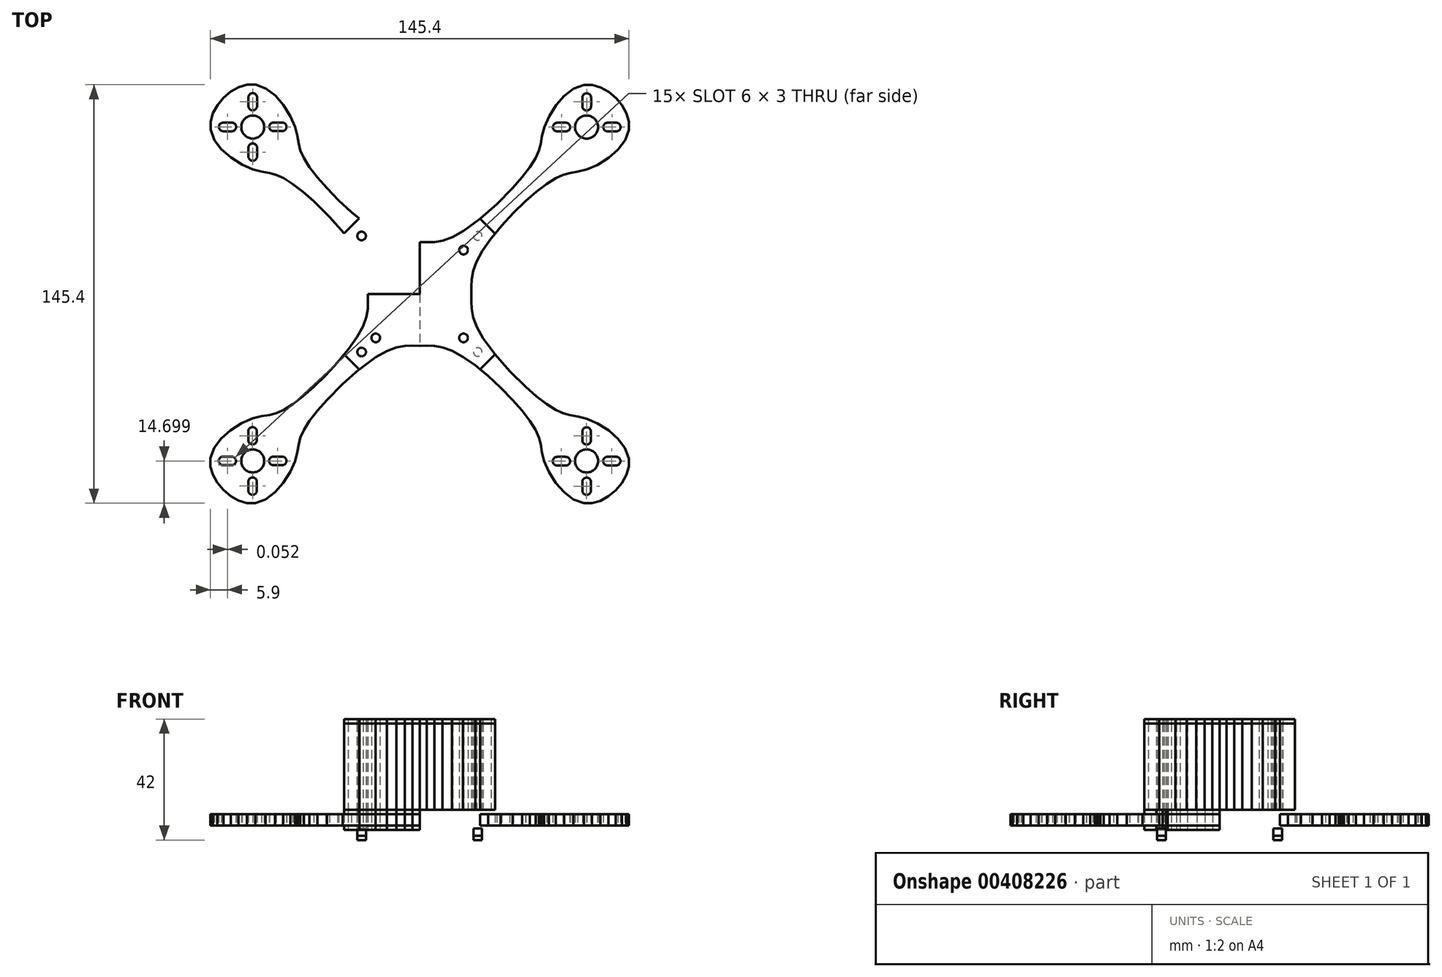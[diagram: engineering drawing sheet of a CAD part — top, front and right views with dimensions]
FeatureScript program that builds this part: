
annotation { "Feature Type Name" : "Feature", "Feature Type Description" : "" }
export const myFeature = defineFeature(function(context is Context, id is Id, definition is map)
    precondition{}
    {
        {
            var Q0;
            Q0=qCreatedBy(makeId("Top.planeOp"),FACE);
            var sketch = newSketch(context, id + "F0", { "sketchPlane" : qUnion([Q0])});
            skCircle(sketch, "E0", {"center": v(20.17, 20.17) * mm, "radius": 1.5 * mm});
            skLineSegment(sketch, "E1", {"start": v(26.23, 21) * mm, "end": v(21.02, 26.2) * mm});
            skLineSegment(sketch, "E2", {"start": v(0, 18) * mm, "end": v(2.5, 17.97) * mm});
            skLineSegment(sketch, "E3", {"start": v(2.5, 17.97) * mm, "end": v(5.15, 18.06) * mm});
            skLineSegment(sketch, "E4", {"start": v(5.15, 18.06) * mm, "end": v(8.09, 18.58) * mm});
            skLineSegment(sketch, "E5", {"start": v(8.09, 18.58) * mm, "end": v(11.44, 19.82) * mm});
            skLineSegment(sketch, "E6", {"start": v(11.44, 19.82) * mm, "end": v(15.32, 22) * mm});
            skLineSegment(sketch, "E7", {"start": v(15.32, 22) * mm, "end": v(20.97, 26.16) * mm});
            skLineSegment(sketch, "E8", {"start": v(20.97, 26.16) * mm, "end": v(26.8, 31.28) * mm});
            skLineSegment(sketch, "E9", {"start": v(26.8, 31.28) * mm, "end": v(32.27, 36.82) * mm});
            skLineSegment(sketch, "E10", {"start": v(32.27, 36.82) * mm, "end": v(35.55, 40.57) * mm});
            skLineSegment(sketch, "E11", {"start": v(35.55, 40.57) * mm, "end": v(38.27, 44.1) * mm});
            skLineSegment(sketch, "E12", {"start": v(38.27, 44.1) * mm, "end": v(40.27, 47.23) * mm});
            skLineSegment(sketch, "E13", {"start": v(40.27, 47.23) * mm, "end": v(41.45, 49.87) * mm});
            skLineSegment(sketch, "E14", {"start": v(41.45, 49.87) * mm, "end": v(42.05, 52.15) * mm});
            skLineSegment(sketch, "E15", {"start": v(42.05, 52.15) * mm, "end": v(42.52, 54.9) * mm});
            skLineSegment(sketch, "E16", {"start": v(42.52, 54.9) * mm, "end": v(43.3, 58) * mm});
            skLineSegment(sketch, "E17", {"start": v(43.3, 58) * mm, "end": v(44.94, 61.72) * mm});
            skLineSegment(sketch, "E18", {"start": v(44.94, 61.72) * mm, "end": v(47.43, 65.67) * mm});
            skLineSegment(sketch, "E19", {"start": v(47.43, 65.67) * mm, "end": v(50.24, 68.86) * mm});
            skLineSegment(sketch, "E20", {"start": v(50.24, 68.86) * mm, "end": v(53.5, 71.33) * mm});
            skLineSegment(sketch, "E21", {"start": v(53.5, 71.33) * mm, "end": v(57.12, 72.65) * mm});
            skLineSegment(sketch, "E22", {"start": v(57.12, 72.65) * mm, "end": v(59.99, 72.64) * mm});
            skLineSegment(sketch, "E23", {"start": v(59.99, 72.64) * mm, "end": v(62.89, 71.79) * mm});
            skLineSegment(sketch, "E24", {"start": v(62.89, 71.79) * mm, "end": v(65.67, 70.23) * mm});
            skLineSegment(sketch, "E25", {"start": v(65.67, 70.23) * mm, "end": v(68.19, 68.12) * mm});
            skLineSegment(sketch, "E26", {"start": v(68.19, 68.12) * mm, "end": v(70.3, 65.6) * mm});
            skLineSegment(sketch, "E27", {"start": v(70.3, 65.6) * mm, "end": v(71.85, 62.8) * mm});
            skLineSegment(sketch, "E28", {"start": v(71.85, 62.8) * mm, "end": v(72.7, 59.9) * mm});
            skLineSegment(sketch, "E29", {"start": v(72.7, 59.9) * mm, "end": v(72.7, 57.03) * mm});
            skLineSegment(sketch, "E30", {"start": v(72.7, 57.03) * mm, "end": v(71.38, 53.41) * mm});
            skLineSegment(sketch, "E31", {"start": v(71.38, 53.41) * mm, "end": v(68.9, 50.15) * mm});
            skLineSegment(sketch, "E32", {"start": v(68.9, 50.15) * mm, "end": v(65.7, 47.34) * mm});
            skLineSegment(sketch, "E33", {"start": v(65.7, 47.34) * mm, "end": v(61.77, 44.86) * mm});
            skLineSegment(sketch, "E34", {"start": v(61.77, 44.86) * mm, "end": v(58.04, 43.24) * mm});
            skLineSegment(sketch, "E35", {"start": v(58.04, 43.24) * mm, "end": v(54.95, 42.47) * mm});
            skLineSegment(sketch, "E36", {"start": v(54.95, 42.47) * mm, "end": v(52.18, 42.03) * mm});
            skLineSegment(sketch, "E37", {"start": v(52.18, 42.03) * mm, "end": v(49.88, 41.44) * mm});
            skLineSegment(sketch, "E38", {"start": v(49.88, 41.44) * mm, "end": v(47.23, 40.27) * mm});
            skLineSegment(sketch, "E39", {"start": v(47.23, 40.27) * mm, "end": v(44.09, 38.28) * mm});
            skLineSegment(sketch, "E40", {"start": v(44.09, 38.28) * mm, "end": v(40.55, 35.56) * mm});
            skLineSegment(sketch, "E41", {"start": v(40.55, 35.56) * mm, "end": v(36.8, 32.28) * mm});
            skLineSegment(sketch, "E42", {"start": v(36.8, 32.28) * mm, "end": v(32.56, 28.14) * mm});
            skLineSegment(sketch, "E43", {"start": v(32.56, 28.14) * mm, "end": v(28.48, 23.74) * mm});
            skLineSegment(sketch, "E44", {"start": v(28.48, 23.74) * mm, "end": v(24.82, 19.29) * mm});
            skLineSegment(sketch, "E45", {"start": v(24.82, 19.29) * mm, "end": v(21.82, 15.03) * mm});
            skLineSegment(sketch, "E46", {"start": v(21.82, 15.03) * mm, "end": v(19.7, 11.19) * mm});
            skLineSegment(sketch, "E47", {"start": v(19.7, 11.19) * mm, "end": v(18.54, 7.93) * mm});
            skLineSegment(sketch, "E48", {"start": v(18.54, 7.93) * mm, "end": v(18.06, 5.07) * mm});
            skLineSegment(sketch, "E49", {"start": v(18.06, 5.07) * mm, "end": v(17.97, 2.47) * mm});
            skLineSegment(sketch, "E50", {"start": v(17.97, 2.47) * mm, "end": v(18, 0) * mm});
            skArc(sketch, "E51", {"start": v(59.58, 50.75) * mm, "mid": v(58.08, 52.25) * mm, "end": v(56.58, 50.75) * mm});
            skArc(sketch, "E52", {"start": v(56.58, 47.75) * mm, "mid": v(58.08, 46.25) * mm, "end": v(59.58, 47.75) * mm});
            skLineSegment(sketch, "E53", {"start": v(59.48, 47.75) * mm, "end": v(59.48, 50.75) * mm});
            skLineSegment(sketch, "E54", {"start": v(56.58, 47.75) * mm, "end": v(56.58, 50.75) * mm});
            skArc(sketch, "E55", {"start": v(65.3, 59.5) * mm, "mid": v(63.8, 58) * mm, "end": v(65.3, 56.5) * mm});
            skArc(sketch, "E56", {"start": v(68.3, 56.5) * mm, "mid": v(69.8, 58) * mm, "end": v(68.3, 59.5) * mm});
            skLineSegment(sketch, "E57", {"start": v(68.3, 59.5) * mm, "end": v(65.3, 59.5) * mm});
            skLineSegment(sketch, "E58", {"start": v(68.3, 56.5) * mm, "end": v(65.3, 56.5) * mm});
            skArc(sketch, "E59", {"start": v(50.8, 56.5) * mm, "mid": v(52.3, 58) * mm, "end": v(50.8, 59.5) * mm});
            skArc(sketch, "E60", {"start": v(47.8, 59.5) * mm, "mid": v(46.3, 58) * mm, "end": v(47.8, 56.5) * mm});
            skLineSegment(sketch, "E61", {"start": v(47.8, 56.5) * mm, "end": v(50.8, 56.5) * mm});
            skLineSegment(sketch, "E62", {"start": v(47.8, 59.5) * mm, "end": v(50.8, 59.5) * mm});
            skArc(sketch, "E63", {"start": v(59.55, 68.25) * mm, "mid": v(58.05, 69.75) * mm, "end": v(56.55, 68.25) * mm});
            skArc(sketch, "E64", {"start": v(56.55, 65.25) * mm, "mid": v(58.05, 63.75) * mm, "end": v(59.55, 65.25) * mm});
            skLineSegment(sketch, "E65", {"start": v(59.55, 65.25) * mm, "end": v(59.55, 68.25) * mm});
            skLineSegment(sketch, "E66", {"start": v(56.55, 65.25) * mm, "end": v(56.55, 68.25) * mm});
            skCircle(sketch, "E67", {"center": v(58, 58) * mm, "radius": 4 * mm});
            skCircle(sketch, "E68", {"center": v(20.17, -20.17) * mm, "radius": 1.5 * mm});
            skCircle(sketch, "E69", {"center": v(-20.17, 20.17) * mm, "radius": 1.5 * mm});
            skLineSegment(sketch, "E70", {"start": v(-21, 26.23) * mm, "end": v(-26.2, 21.02) * mm});
            skLineSegment(sketch, "E71", {"start": v(-18, 0) * mm, "end": v(-17.97, 2.5) * mm});
            skLineSegment(sketch, "E72", {"start": v(-17.97, 2.5) * mm, "end": v(-18.06, 5.15) * mm});
            skLineSegment(sketch, "E73", {"start": v(-18.06, 5.15) * mm, "end": v(-18.58, 8.09) * mm});
            skLineSegment(sketch, "E74", {"start": v(-18.58, 8.09) * mm, "end": v(-19.81, 11.44) * mm});
            skLineSegment(sketch, "E75", {"start": v(-19.81, 11.44) * mm, "end": v(-22, 15.32) * mm});
            skLineSegment(sketch, "E76", {"start": v(-22, 15.32) * mm, "end": v(-26.16, 20.97) * mm});
            skLineSegment(sketch, "E77", {"start": v(-26.16, 20.97) * mm, "end": v(-31.28, 26.8) * mm});
            skLineSegment(sketch, "E78", {"start": v(-31.28, 26.8) * mm, "end": v(-36.82, 32.27) * mm});
            skLineSegment(sketch, "E79", {"start": v(-36.82, 32.27) * mm, "end": v(-40.57, 35.55) * mm});
            skLineSegment(sketch, "E80", {"start": v(-40.57, 35.55) * mm, "end": v(-44.1, 38.27) * mm});
            skLineSegment(sketch, "E81", {"start": v(-44.1, 38.27) * mm, "end": v(-47.23, 40.27) * mm});
            skLineSegment(sketch, "E82", {"start": v(-47.23, 40.27) * mm, "end": v(-49.87, 41.45) * mm});
            skLineSegment(sketch, "E83", {"start": v(-49.87, 41.45) * mm, "end": v(-52.15, 42.05) * mm});
            skLineSegment(sketch, "E84", {"start": v(-52.15, 42.05) * mm, "end": v(-54.9, 42.52) * mm});
            skLineSegment(sketch, "E85", {"start": v(-54.9, 42.52) * mm, "end": v(-58, 43.3) * mm});
            skLineSegment(sketch, "E86", {"start": v(-58, 43.3) * mm, "end": v(-61.72, 44.94) * mm});
            skLineSegment(sketch, "E87", {"start": v(-61.72, 44.94) * mm, "end": v(-65.66, 47.43) * mm});
            skLineSegment(sketch, "E88", {"start": v(-65.66, 47.43) * mm, "end": v(-68.86, 50.24) * mm});
            skLineSegment(sketch, "E89", {"start": v(-68.86, 50.24) * mm, "end": v(-71.33, 53.5) * mm});
            skLineSegment(sketch, "E90", {"start": v(-71.33, 53.5) * mm, "end": v(-72.65, 57.12) * mm});
            skLineSegment(sketch, "E91", {"start": v(-72.65, 57.12) * mm, "end": v(-72.64, 60) * mm});
            skLineSegment(sketch, "E92", {"start": v(-72.64, 60) * mm, "end": v(-71.79, 62.9) * mm});
            skLineSegment(sketch, "E93", {"start": v(-71.79, 62.9) * mm, "end": v(-70.23, 65.67) * mm});
            skLineSegment(sketch, "E94", {"start": v(-70.23, 65.67) * mm, "end": v(-68.12, 68.2) * mm});
            skLineSegment(sketch, "E95", {"start": v(-68.12, 68.2) * mm, "end": v(-65.6, 70.3) * mm});
            skLineSegment(sketch, "E96", {"start": v(-65.6, 70.3) * mm, "end": v(-62.8, 71.85) * mm});
            skLineSegment(sketch, "E97", {"start": v(-62.8, 71.85) * mm, "end": v(-59.9, 72.7) * mm});
            skLineSegment(sketch, "E98", {"start": v(-59.9, 72.7) * mm, "end": v(-57.03, 72.7) * mm});
            skLineSegment(sketch, "E99", {"start": v(-57.03, 72.7) * mm, "end": v(-53.41, 71.38) * mm});
            skLineSegment(sketch, "E100", {"start": v(-53.41, 71.38) * mm, "end": v(-50.15, 68.9) * mm});
            skLineSegment(sketch, "E101", {"start": v(-50.15, 68.9) * mm, "end": v(-47.34, 65.7) * mm});
            skLineSegment(sketch, "E102", {"start": v(-47.34, 65.7) * mm, "end": v(-44.86, 61.77) * mm});
            skLineSegment(sketch, "E103", {"start": v(-44.86, 61.77) * mm, "end": v(-43.23, 58.04) * mm});
            skLineSegment(sketch, "E104", {"start": v(-43.23, 58.04) * mm, "end": v(-42.47, 54.95) * mm});
            skLineSegment(sketch, "E105", {"start": v(-42.47, 54.95) * mm, "end": v(-42.03, 52.18) * mm});
            skLineSegment(sketch, "E106", {"start": v(-42.03, 52.18) * mm, "end": v(-41.44, 49.88) * mm});
            skLineSegment(sketch, "E107", {"start": v(-41.44, 49.88) * mm, "end": v(-40.27, 47.23) * mm});
            skLineSegment(sketch, "E108", {"start": v(-40.27, 47.23) * mm, "end": v(-38.28, 44.09) * mm});
            skLineSegment(sketch, "E109", {"start": v(-38.28, 44.09) * mm, "end": v(-35.56, 40.55) * mm});
            skLineSegment(sketch, "E110", {"start": v(-35.56, 40.55) * mm, "end": v(-32.28, 36.8) * mm});
            skLineSegment(sketch, "E111", {"start": v(-32.28, 36.8) * mm, "end": v(-28.14, 32.56) * mm});
            skLineSegment(sketch, "E112", {"start": v(-28.14, 32.56) * mm, "end": v(-23.73, 28.48) * mm});
            skLineSegment(sketch, "E113", {"start": v(-23.73, 28.48) * mm, "end": v(-19.29, 24.83) * mm});
            skLineSegment(sketch, "E114", {"start": v(-19.29, 24.83) * mm, "end": v(-15.03, 21.82) * mm});
            skLineSegment(sketch, "E115", {"start": v(-15.03, 21.82) * mm, "end": v(-11.19, 19.7) * mm});
            skLineSegment(sketch, "E116", {"start": v(-11.19, 19.7) * mm, "end": v(-7.93, 18.54) * mm});
            skLineSegment(sketch, "E117", {"start": v(-7.93, 18.54) * mm, "end": v(-5.07, 18.06) * mm});
            skLineSegment(sketch, "E118", {"start": v(-5.07, 18.06) * mm, "end": v(-2.47, 17.97) * mm});
            skLineSegment(sketch, "E119", {"start": v(-2.47, 17.97) * mm, "end": v(0, 18) * mm});
            skArc(sketch, "E120", {"start": v(-50.75, 59.58) * mm, "mid": v(-52.25, 58.08) * mm, "end": v(-50.75, 56.58) * mm});
            skArc(sketch, "E121", {"start": v(-47.75, 56.58) * mm, "mid": v(-46.25, 58.08) * mm, "end": v(-47.75, 59.58) * mm});
            skLineSegment(sketch, "E122", {"start": v(-47.75, 59.58) * mm, "end": v(-50.75, 59.58) * mm});
            skLineSegment(sketch, "E123", {"start": v(-47.75, 56.58) * mm, "end": v(-50.75, 56.58) * mm});
            skArc(sketch, "E124", {"start": v(-59.5, 65.3) * mm, "mid": v(-58, 63.8) * mm, "end": v(-56.5, 65.3) * mm});
            skArc(sketch, "E125", {"start": v(-56.5, 68.3) * mm, "mid": v(-58, 69.8) * mm, "end": v(-59.5, 68.3) * mm});
            skLineSegment(sketch, "E126", {"start": v(-59.5, 68.3) * mm, "end": v(-59.5, 65.3) * mm});
            skLineSegment(sketch, "E127", {"start": v(-56.5, 68.3) * mm, "end": v(-56.5, 65.3) * mm});
            skArc(sketch, "E128", {"start": v(-56.5, 50.8) * mm, "mid": v(-58, 52.3) * mm, "end": v(-59.5, 50.8) * mm});
            skArc(sketch, "E129", {"start": v(-59.5, 47.8) * mm, "mid": v(-58, 46.3) * mm, "end": v(-56.5, 47.8) * mm});
            skLineSegment(sketch, "E130", {"start": v(-56.5, 47.8) * mm, "end": v(-56.5, 50.8) * mm});
            skLineSegment(sketch, "E131", {"start": v(-59.5, 47.8) * mm, "end": v(-59.5, 50.8) * mm});
            skArc(sketch, "E132", {"start": v(-68.25, 59.55) * mm, "mid": v(-69.75, 58.05) * mm, "end": v(-68.25, 56.55) * mm});
            skArc(sketch, "E133", {"start": v(-65.25, 56.55) * mm, "mid": v(-63.75, 58.05) * mm, "end": v(-65.25, 59.55) * mm});
            skLineSegment(sketch, "E134", {"start": v(-65.25, 59.55) * mm, "end": v(-68.25, 59.55) * mm});
            skLineSegment(sketch, "E135", {"start": v(-65.25, 56.55) * mm, "end": v(-68.25, 56.55) * mm});
            skCircle(sketch, "E136", {"center": v(-58, 58) * mm, "radius": 4 * mm});
            skLineSegment(sketch, "E137", {"start": v(20.99, -26.22) * mm, "end": v(26.2, -21.02) * mm});
            skLineSegment(sketch, "E138", {"start": v(18, 0) * mm, "end": v(17.97, -2.5) * mm});
            skLineSegment(sketch, "E139", {"start": v(17.97, -2.5) * mm, "end": v(18.07, -5.15) * mm});
            skLineSegment(sketch, "E140", {"start": v(18.07, -5.15) * mm, "end": v(18.58, -8.09) * mm});
            skLineSegment(sketch, "E141", {"start": v(18.58, -8.09) * mm, "end": v(19.82, -11.44) * mm});
            skLineSegment(sketch, "E142", {"start": v(19.82, -11.44) * mm, "end": v(22.01, -15.32) * mm});
            skLineSegment(sketch, "E143", {"start": v(22.01, -15.32) * mm, "end": v(26.16, -20.97) * mm});
            skLineSegment(sketch, "E144", {"start": v(26.16, -20.97) * mm, "end": v(31.28, -26.8) * mm});
            skLineSegment(sketch, "E145", {"start": v(31.28, -26.8) * mm, "end": v(36.82, -32.27) * mm});
            skLineSegment(sketch, "E146", {"start": v(36.82, -32.27) * mm, "end": v(40.57, -35.55) * mm});
            skLineSegment(sketch, "E147", {"start": v(40.57, -35.55) * mm, "end": v(44.1, -38.27) * mm});
            skLineSegment(sketch, "E148", {"start": v(44.1, -38.27) * mm, "end": v(47.24, -40.27) * mm});
            skLineSegment(sketch, "E149", {"start": v(47.24, -40.27) * mm, "end": v(49.87, -41.45) * mm});
            skLineSegment(sketch, "E150", {"start": v(49.87, -41.45) * mm, "end": v(52.16, -42.05) * mm});
            skLineSegment(sketch, "E151", {"start": v(52.16, -42.05) * mm, "end": v(54.9, -42.52) * mm});
            skLineSegment(sketch, "E152", {"start": v(54.9, -42.52) * mm, "end": v(58, -43.3) * mm});
            skLineSegment(sketch, "E153", {"start": v(58, -43.3) * mm, "end": v(61.72, -44.94) * mm});
            skLineSegment(sketch, "E154", {"start": v(61.72, -44.94) * mm, "end": v(65.67, -47.43) * mm});
            skLineSegment(sketch, "E155", {"start": v(65.67, -47.43) * mm, "end": v(68.87, -50.24) * mm});
            skLineSegment(sketch, "E156", {"start": v(68.87, -50.24) * mm, "end": v(71.34, -53.5) * mm});
            skLineSegment(sketch, "E157", {"start": v(71.34, -53.5) * mm, "end": v(72.65, -57.12) * mm});
            skLineSegment(sketch, "E158", {"start": v(72.65, -57.12) * mm, "end": v(72.64, -60) * mm});
            skLineSegment(sketch, "E159", {"start": v(72.64, -60) * mm, "end": v(71.79, -62.9) * mm});
            skLineSegment(sketch, "E160", {"start": v(71.79, -62.9) * mm, "end": v(70.23, -65.67) * mm});
            skLineSegment(sketch, "E161", {"start": v(70.23, -65.67) * mm, "end": v(68.12, -68.2) * mm});
            skLineSegment(sketch, "E162", {"start": v(68.12, -68.2) * mm, "end": v(65.6, -70.3) * mm});
            skLineSegment(sketch, "E163", {"start": v(65.6, -70.3) * mm, "end": v(62.8, -71.85) * mm});
            skLineSegment(sketch, "E164", {"start": v(62.8, -71.85) * mm, "end": v(59.9, -72.7) * mm});
            skLineSegment(sketch, "E165", {"start": v(59.9, -72.7) * mm, "end": v(57.03, -72.7) * mm});
            skLineSegment(sketch, "E166", {"start": v(57.03, -72.7) * mm, "end": v(53.41, -71.38) * mm});
            skLineSegment(sketch, "E167", {"start": v(53.41, -71.38) * mm, "end": v(50.15, -68.9) * mm});
            skLineSegment(sketch, "E168", {"start": v(50.15, -68.9) * mm, "end": v(47.34, -65.7) * mm});
            skLineSegment(sketch, "E169", {"start": v(47.34, -65.7) * mm, "end": v(44.86, -61.77) * mm});
            skLineSegment(sketch, "E170", {"start": v(44.86, -61.77) * mm, "end": v(43.24, -58.04) * mm});
            skLineSegment(sketch, "E171", {"start": v(43.24, -58.04) * mm, "end": v(42.47, -54.95) * mm});
            skLineSegment(sketch, "E172", {"start": v(42.47, -54.95) * mm, "end": v(42.03, -52.18) * mm});
            skLineSegment(sketch, "E173", {"start": v(42.03, -52.18) * mm, "end": v(41.44, -49.88) * mm});
            skLineSegment(sketch, "E174", {"start": v(41.44, -49.88) * mm, "end": v(40.27, -47.23) * mm});
            skLineSegment(sketch, "E175", {"start": v(40.27, -47.23) * mm, "end": v(38.28, -44.09) * mm});
            skLineSegment(sketch, "E176", {"start": v(38.28, -44.09) * mm, "end": v(35.56, -40.55) * mm});
            skLineSegment(sketch, "E177", {"start": v(35.56, -40.55) * mm, "end": v(32.28, -36.8) * mm});
            skLineSegment(sketch, "E178", {"start": v(32.28, -36.8) * mm, "end": v(28.14, -32.56) * mm});
            skLineSegment(sketch, "E179", {"start": v(28.14, -32.56) * mm, "end": v(23.74, -28.48) * mm});
            skLineSegment(sketch, "E180", {"start": v(23.74, -28.48) * mm, "end": v(19.29, -24.83) * mm});
            skLineSegment(sketch, "E181", {"start": v(19.29, -24.83) * mm, "end": v(15.03, -21.82) * mm});
            skLineSegment(sketch, "E182", {"start": v(15.03, -21.82) * mm, "end": v(11.2, -19.7) * mm});
            skLineSegment(sketch, "E183", {"start": v(11.2, -19.7) * mm, "end": v(7.93, -18.54) * mm});
            skLineSegment(sketch, "E184", {"start": v(7.93, -18.54) * mm, "end": v(5.07, -18.06) * mm});
            skLineSegment(sketch, "E185", {"start": v(5.07, -18.06) * mm, "end": v(2.47, -17.97) * mm});
            skLineSegment(sketch, "E186", {"start": v(2.47, -17.97) * mm, "end": v(0, -18) * mm});
            skArc(sketch, "E187", {"start": v(50.75, -59.58) * mm, "mid": v(52.25, -58.08) * mm, "end": v(50.75, -56.58) * mm});
            skArc(sketch, "E188", {"start": v(47.75, -56.58) * mm, "mid": v(46.25, -58.08) * mm, "end": v(47.75, -59.58) * mm});
            skLineSegment(sketch, "E189", {"start": v(47.75, -59.58) * mm, "end": v(50.75, -59.58) * mm});
            skLineSegment(sketch, "E190", {"start": v(47.75, -56.58) * mm, "end": v(50.75, -56.58) * mm});
            skArc(sketch, "E191", {"start": v(59.5, -65.3) * mm, "mid": v(58, -63.8) * mm, "end": v(56.5, -65.3) * mm});
            skArc(sketch, "E192", {"start": v(56.5, -68.3) * mm, "mid": v(58, -69.8) * mm, "end": v(59.5, -68.3) * mm});
            skLineSegment(sketch, "E193", {"start": v(59.5, -68.3) * mm, "end": v(59.5, -65.3) * mm});
            skLineSegment(sketch, "E194", {"start": v(56.5, -68.3) * mm, "end": v(56.5, -65.3) * mm});
            skArc(sketch, "E195", {"start": v(56.5, -50.8) * mm, "mid": v(58, -52.3) * mm, "end": v(59.5, -50.8) * mm});
            skArc(sketch, "E196", {"start": v(59.5, -47.8) * mm, "mid": v(58, -46.3) * mm, "end": v(56.5, -47.8) * mm});
            skLineSegment(sketch, "E197", {"start": v(56.5, -47.8) * mm, "end": v(56.5, -50.8) * mm});
            skLineSegment(sketch, "E198", {"start": v(59.5, -47.8) * mm, "end": v(59.5, -50.8) * mm});
            skArc(sketch, "E199", {"start": v(68.25, -59.55) * mm, "mid": v(69.75, -58.05) * mm, "end": v(68.25, -56.55) * mm});
            skArc(sketch, "E200", {"start": v(65.25, -56.55) * mm, "mid": v(63.75, -58.05) * mm, "end": v(65.25, -59.55) * mm});
            skLineSegment(sketch, "E201", {"start": v(65.25, -59.55) * mm, "end": v(68.25, -59.55) * mm});
            skLineSegment(sketch, "E202", {"start": v(65.25, -56.55) * mm, "end": v(68.25, -56.55) * mm});
            skCircle(sketch, "E203", {"center": v(58, -58) * mm, "radius": 4 * mm});
            skLineSegment(sketch, "E204", {"start": v(-18, 0) * mm, "end": v(0, 0) * mm});
            skLineSegment(sketch, "E205", {"start": v(-26.23, -21) * mm, "end": v(-21.02, -26.2) * mm});
            skLineSegment(sketch, "E206", {"start": v(0, -18) * mm, "end": v(-2.5, -17.97) * mm});
            skLineSegment(sketch, "E207", {"start": v(-2.5, -17.97) * mm, "end": v(-5.15, -18.06) * mm});
            skLineSegment(sketch, "E208", {"start": v(-5.15, -18.06) * mm, "end": v(-8.09, -18.58) * mm});
            skLineSegment(sketch, "E209", {"start": v(-8.09, -18.58) * mm, "end": v(-11.44, -19.82) * mm});
            skLineSegment(sketch, "E210", {"start": v(-11.44, -19.82) * mm, "end": v(-15.32, -22) * mm});
            skLineSegment(sketch, "E211", {"start": v(-15.32, -22) * mm, "end": v(-20.97, -26.16) * mm});
            skLineSegment(sketch, "E212", {"start": v(-20.97, -26.16) * mm, "end": v(-26.8, -31.28) * mm});
            skLineSegment(sketch, "E213", {"start": v(-26.8, -31.28) * mm, "end": v(-32.27, -36.82) * mm});
            skLineSegment(sketch, "E214", {"start": v(-32.27, -36.82) * mm, "end": v(-35.55, -40.57) * mm});
            skLineSegment(sketch, "E215", {"start": v(-35.55, -40.57) * mm, "end": v(-38.27, -44.1) * mm});
            skLineSegment(sketch, "E216", {"start": v(-38.27, -44.1) * mm, "end": v(-40.27, -47.23) * mm});
            skLineSegment(sketch, "E217", {"start": v(-40.27, -47.23) * mm, "end": v(-41.45, -49.87) * mm});
            skLineSegment(sketch, "E218", {"start": v(-41.45, -49.87) * mm, "end": v(-42.05, -52.15) * mm});
            skLineSegment(sketch, "E219", {"start": v(-42.05, -52.15) * mm, "end": v(-42.52, -54.9) * mm});
            skLineSegment(sketch, "E220", {"start": v(-42.52, -54.9) * mm, "end": v(-43.3, -58) * mm});
            skLineSegment(sketch, "E221", {"start": v(-43.3, -58) * mm, "end": v(-44.94, -61.72) * mm});
            skLineSegment(sketch, "E222", {"start": v(-44.94, -61.72) * mm, "end": v(-47.43, -65.67) * mm});
            skLineSegment(sketch, "E223", {"start": v(-47.43, -65.67) * mm, "end": v(-50.24, -68.86) * mm});
            skLineSegment(sketch, "E224", {"start": v(-50.24, -68.86) * mm, "end": v(-53.5, -71.33) * mm});
            skLineSegment(sketch, "E225", {"start": v(-53.5, -71.33) * mm, "end": v(-57.12, -72.65) * mm});
            skLineSegment(sketch, "E226", {"start": v(-57.12, -72.65) * mm, "end": v(-59.99, -72.64) * mm});
            skLineSegment(sketch, "E227", {"start": v(-59.99, -72.64) * mm, "end": v(-62.89, -71.79) * mm});
            skLineSegment(sketch, "E228", {"start": v(-62.89, -71.79) * mm, "end": v(-65.67, -70.23) * mm});
            skLineSegment(sketch, "E229", {"start": v(-65.67, -70.23) * mm, "end": v(-68.19, -68.12) * mm});
            skLineSegment(sketch, "E230", {"start": v(-68.19, -68.12) * mm, "end": v(-70.3, -65.6) * mm});
            skLineSegment(sketch, "E231", {"start": v(-70.3, -65.6) * mm, "end": v(-71.85, -62.8) * mm});
            skLineSegment(sketch, "E232", {"start": v(-71.85, -62.8) * mm, "end": v(-72.7, -59.9) * mm});
            skLineSegment(sketch, "E233", {"start": v(-72.7, -59.9) * mm, "end": v(-72.7, -57.03) * mm});
            skLineSegment(sketch, "E234", {"start": v(-72.7, -57.03) * mm, "end": v(-71.38, -53.41) * mm});
            skLineSegment(sketch, "E235", {"start": v(-71.38, -53.41) * mm, "end": v(-68.9, -50.15) * mm});
            skLineSegment(sketch, "E236", {"start": v(-68.9, -50.15) * mm, "end": v(-65.7, -47.34) * mm});
            skLineSegment(sketch, "E237", {"start": v(-65.7, -47.34) * mm, "end": v(-61.77, -44.86) * mm});
            skLineSegment(sketch, "E238", {"start": v(-61.77, -44.86) * mm, "end": v(-58.04, -43.24) * mm});
            skLineSegment(sketch, "E239", {"start": v(-58.04, -43.24) * mm, "end": v(-54.95, -42.47) * mm});
            skLineSegment(sketch, "E240", {"start": v(-54.95, -42.47) * mm, "end": v(-52.18, -42.03) * mm});
            skLineSegment(sketch, "E241", {"start": v(-52.18, -42.03) * mm, "end": v(-49.88, -41.44) * mm});
            skLineSegment(sketch, "E242", {"start": v(-49.88, -41.44) * mm, "end": v(-47.23, -40.27) * mm});
            skLineSegment(sketch, "E243", {"start": v(-47.23, -40.27) * mm, "end": v(-44.09, -38.28) * mm});
            skLineSegment(sketch, "E244", {"start": v(-44.09, -38.28) * mm, "end": v(-40.55, -35.56) * mm});
            skLineSegment(sketch, "E245", {"start": v(-40.55, -35.56) * mm, "end": v(-36.8, -32.28) * mm});
            skLineSegment(sketch, "E246", {"start": v(-36.8, -32.28) * mm, "end": v(-32.56, -28.14) * mm});
            skLineSegment(sketch, "E247", {"start": v(-32.56, -28.14) * mm, "end": v(-28.48, -23.74) * mm});
            skLineSegment(sketch, "E248", {"start": v(-28.48, -23.74) * mm, "end": v(-24.82, -19.29) * mm});
            skLineSegment(sketch, "E249", {"start": v(-24.82, -19.29) * mm, "end": v(-21.82, -15.03) * mm});
            skLineSegment(sketch, "E250", {"start": v(-21.82, -15.03) * mm, "end": v(-19.7, -11.19) * mm});
            skLineSegment(sketch, "E251", {"start": v(-19.7, -11.19) * mm, "end": v(-18.54, -7.93) * mm});
            skLineSegment(sketch, "E252", {"start": v(-18.54, -7.93) * mm, "end": v(-18.06, -5.07) * mm});
            skLineSegment(sketch, "E253", {"start": v(-18.06, -5.07) * mm, "end": v(-17.97, -2.47) * mm});
            skLineSegment(sketch, "E254", {"start": v(-17.97, -2.47) * mm, "end": v(-18, 0) * mm});
            skArc(sketch, "E255", {"start": v(-59.58, -50.75) * mm, "mid": v(-58.08, -52.25) * mm, "end": v(-56.58, -50.75) * mm});
            skArc(sketch, "E256", {"start": v(-56.58, -47.75) * mm, "mid": v(-58.08, -46.25) * mm, "end": v(-59.58, -47.75) * mm});
            skLineSegment(sketch, "E257", {"start": v(-59.58, -47.75) * mm, "end": v(-59.58, -50.75) * mm});
            skLineSegment(sketch, "E258", {"start": v(-56.58, -47.75) * mm, "end": v(-56.58, -50.75) * mm});
            skArc(sketch, "E259", {"start": v(-65.3, -59.5) * mm, "mid": v(-63.8, -58) * mm, "end": v(-65.3, -56.5) * mm});
            skArc(sketch, "E260", {"start": v(-68.3, -56.5) * mm, "mid": v(-69.8, -58) * mm, "end": v(-68.3, -59.5) * mm});
            skLineSegment(sketch, "E261", {"start": v(-68.3, -59.5) * mm, "end": v(-65.3, -59.5) * mm});
            skLineSegment(sketch, "E262", {"start": v(-68.3, -56.5) * mm, "end": v(-65.3, -56.5) * mm});
            skArc(sketch, "E263", {"start": v(-50.8, -56.5) * mm, "mid": v(-52.3, -58) * mm, "end": v(-50.8, -59.5) * mm});
            skArc(sketch, "E264", {"start": v(-47.8, -59.5) * mm, "mid": v(-46.3, -58) * mm, "end": v(-47.8, -56.5) * mm});
            skLineSegment(sketch, "E265", {"start": v(-47.8, -56.5) * mm, "end": v(-50.8, -56.5) * mm});
            skLineSegment(sketch, "E266", {"start": v(-47.8, -59.5) * mm, "end": v(-50.8, -59.5) * mm});
            skArc(sketch, "E267", {"start": v(-59.55, -68.25) * mm, "mid": v(-58.05, -69.75) * mm, "end": v(-56.55, -68.25) * mm});
            skArc(sketch, "E268", {"start": v(-56.55, -65.25) * mm, "mid": v(-58.05, -63.75) * mm, "end": v(-59.55, -65.25) * mm});
            skLineSegment(sketch, "E269", {"start": v(-59.55, -65.25) * mm, "end": v(-59.55, -68.25) * mm});
            skLineSegment(sketch, "E270", {"start": v(-56.55, -65.25) * mm, "end": v(-56.55, -68.25) * mm});
            skCircle(sketch, "E271", {"center": v(-58, -58) * mm, "radius": 4 * mm});
            skLineSegment(sketch, "E272", {"start": v(0, 0) * mm, "end": v(0, -18) * mm});
            skCircle(sketch, "E273", {"center": v(-20.17, -20.17) * mm, "radius": 1.5 * mm});
            skCircle(sketch, "E274", {"center": v(15.25, 15.25) * mm, "radius": 1.5 * mm});
            skCircle(sketch, "E275", {"center": v(15.25, -15.25) * mm, "radius": 1.5 * mm});
            skCircle(sketch, "E276", {"center": v(-15.25, -15.25) * mm, "radius": 1.5 * mm});
            skCircle(sketch, "E277", {"center": v(-15.25, 16.63) * mm, "radius": 1.5 * mm});
            skLineSegment(sketch, "E278", {"start": v(0, 0) * mm, "end": v(0, 18) * mm});
            skLineSegment(sketch, "E279", {"start": v(0, 0) * mm, "end": v(18, 0) * mm});
            skPoint(sketch, "E280", {"position": v(-15.25, -10.25) * mm});
            skLineSegment(sketch, "E281.top", {"start": v(-15.06, 0) * mm, "end": v(-12.17, 0) * mm});
            skPoint(sketch, "E282", {"position": v(49.3, 58) * mm});
            skSolve(sketch);
        }
        {
            var Q0;
            {var subQ1=sQuery(id+"F0.wireOp",EDGE,"E205");Q0=makeQuery(id+"F0.imprint","IMPRINT",FACE,{"disambiguationData":[TD([[makeQuery(id+"F0.imprint","IMPRINT",EDGE,{"derivedFrom":subQ1}),1.0]])]});}
            var Q1;
            {var subQ1=sQuery(id+"F0.wireOp",EDGE,"E205");Q1=makeQuery(id+"F0.imprint","IMPRINT",FACE,{"disambiguationData":[TD([[makeQuery(id+"F0.imprint","IMPRINT",EDGE,{"derivedFrom":subQ1}),-1.0]])]});}
            extrude(context, id + "F1", {"entities" : qUnion([Q0, Q1]), "depth" : 4 * mm});
        }
        {
            var Q0;
            Q0=makeQuery(id+"F0.imprint","IMPRINT",FACE,{"disambiguationData":[TD([[makeQuery(id+"F0.imprint","IMPRINT",EDGE,{"derivedFrom":sQuery(id+"F0.wireOp",EDGE,"E69")}),1.0]])]});
            var Q1;
            {var subQ1=sQuery(id+"F0.wireOp",EDGE,"E70");Q1=makeQuery(id+"F0.imprint","IMPRINT",FACE,{"disambiguationData":[TD([[makeQuery(id+"F0.imprint","IMPRINT",EDGE,{"derivedFrom":subQ1}),-1.0]])]});}
            extrude(context, id + "F2", {"entities" : qUnion([Q0, Q1]), "depth" : 4 * mm});
        }
        {
            var Q0;
            Q0=makeQuery(id+"F0.imprint","IMPRINT",FACE,{"disambiguationData":[TD([[makeQuery(id+"F0.imprint","IMPRINT",EDGE,{"derivedFrom":sQuery(id+"F0.wireOp",EDGE,"E0")}),1.0]])]});
            var Q1;
            {var subQ1=sQuery(id+"F0.wireOp",EDGE,"E1");Q1=makeQuery(id+"F0.imprint","IMPRINT",FACE,{"disambiguationData":[TD([[makeQuery(id+"F0.imprint","IMPRINT",EDGE,{"derivedFrom":subQ1}),-1.0]])]});}
            extrude(context, id + "F3", {"entities" : qUnion([Q0, Q1]), "depth" : 4 * mm});
        }
        {
            var Q0;
            Q0=makeQuery(id+"F0.imprint","IMPRINT",FACE,{"disambiguationData":[TD([[makeQuery(id+"F0.imprint","IMPRINT",EDGE,{"derivedFrom":sQuery(id+"F0.wireOp",EDGE,"E68")}),1.0]])]});
            var Q1;
            {var subQ1=sQuery(id+"F0.wireOp",EDGE,"E137");Q1=makeQuery(id+"F0.imprint","IMPRINT",FACE,{"disambiguationData":[TD([[makeQuery(id+"F0.imprint","IMPRINT",EDGE,{"derivedFrom":subQ1}),-1.0]])]});}
            extrude(context, id + "F4", {"entities" : qUnion([Q0, Q1]), "depth" : 4 * mm});
        }
        {
            var Q0;
            Q0=makeQuery(id+"F0.imprint","IMPRINT",FACE,{"disambiguationData":[TD([[makeQuery(id+"F0.imprint","IMPRINT",EDGE,{"derivedFrom":sQuery(id+"F0.wireOp",EDGE,"E69")}),1.0]])]});
            var Q1;
            Q1=makeQuery(id+"F0.imprint","IMPRINT",FACE,{"disambiguationData":[TD([[makeQuery(id+"F0.imprint","IMPRINT",EDGE,{"derivedFrom":sQuery(id+"F0.wireOp",EDGE,"E0")}),1.0]])]});
            var Q2;
            Q2=makeQuery(id+"F0.imprint","IMPRINT",FACE,{"disambiguationData":[TD([[makeQuery(id+"F0.imprint","IMPRINT",EDGE,{"derivedFrom":sQuery(id+"F0.wireOp",EDGE,"E68")}),1.0]])]});
            var Q3;
            {var subQ1=sQuery(id+"F0.wireOp",EDGE,"E205");Q3=makeQuery(id+"F0.imprint","IMPRINT",FACE,{"disambiguationData":[TD([[makeQuery(id+"F0.imprint","IMPRINT",EDGE,{"derivedFrom":subQ1}),1.0]])]});}
            extrude(context, id + "F5", {"entities" : qUnion([Q0, Q1, Q2, Q3]), "depth" : 1.5 * mm});
        }
        {
            var Q0;
            Q0=makeQuery(id+"F5.opExtrude","CAP_FACE",FACE,{"disambiguationData":[OSD([sQuery(id+"F0.wireOp",EDGE,"E0"),sQuery(id+"F0.wireOp",EDGE,"E1"),sQuery(id+"F0.wireOp",EDGE,"E2"),sQuery(id+"F0.wireOp",EDGE,"E3"),sQuery(id+"F0.wireOp",EDGE,"E4"),sQuery(id+"F0.wireOp",EDGE,"E5"),sQuery(id+"F0.wireOp",EDGE,"E6"),sQuery(id+"F0.wireOp",EDGE,"E7"),sQuery(id+"F0.wireOp",EDGE,"E8"),sQuery(id+"F0.wireOp",EDGE,"E44"),sQuery(id+"F0.wireOp",EDGE,"E45"),sQuery(id+"F0.wireOp",EDGE,"E46"),sQuery(id+"F0.wireOp",EDGE,"E47"),sQuery(id+"F0.wireOp",EDGE,"E48"),sQuery(id+"F0.wireOp",EDGE,"E49"),sQuery(id+"F0.wireOp",EDGE,"E50"),sQuery(id+"F0.wireOp",EDGE,"E68"),sQuery(id+"F0.wireOp",EDGE,"E69"),sQuery(id+"F0.wireOp",EDGE,"E70"),sQuery(id+"F0.wireOp",EDGE,"E71"),sQuery(id+"F0.wireOp",EDGE,"E72"),sQuery(id+"F0.wireOp",EDGE,"E73"),sQuery(id+"F0.wireOp",EDGE,"E74"),sQuery(id+"F0.wireOp",EDGE,"E75"),sQuery(id+"F0.wireOp",EDGE,"E76"),sQuery(id+"F0.wireOp",EDGE,"E77"),sQuery(id+"F0.wireOp",EDGE,"E113"),sQuery(id+"F0.wireOp",EDGE,"E114"),sQuery(id+"F0.wireOp",EDGE,"E115"),sQuery(id+"F0.wireOp",EDGE,"E116"),sQuery(id+"F0.wireOp",EDGE,"E117"),sQuery(id+"F0.wireOp",EDGE,"E118"),sQuery(id+"F0.wireOp",EDGE,"E119"),sQuery(id+"F0.wireOp",EDGE,"E137"),sQuery(id+"F0.wireOp",EDGE,"E138"),sQuery(id+"F0.wireOp",EDGE,"E139"),sQuery(id+"F0.wireOp",EDGE,"E140"),sQuery(id+"F0.wireOp",EDGE,"E141"),sQuery(id+"F0.wireOp",EDGE,"E142"),sQuery(id+"F0.wireOp",EDGE,"E143"),sQuery(id+"F0.wireOp",EDGE,"E144"),sQuery(id+"F0.wireOp",EDGE,"E180"),sQuery(id+"F0.wireOp",EDGE,"E181"),sQuery(id+"F0.wireOp",EDGE,"E182"),sQuery(id+"F0.wireOp",EDGE,"E183"),sQuery(id+"F0.wireOp",EDGE,"E184"),sQuery(id+"F0.wireOp",EDGE,"E185"),sQuery(id+"F0.wireOp",EDGE,"E186"),sQuery(id+"F0.wireOp",EDGE,"E204"),sQuery(id+"F0.wireOp",EDGE,"E205"),sQuery(id+"F0.wireOp",EDGE,"E206"),sQuery(id+"F0.wireOp",EDGE,"E207"),sQuery(id+"F0.wireOp",EDGE,"E208"),sQuery(id+"F0.wireOp",EDGE,"E209"),sQuery(id+"F0.wireOp",EDGE,"E210"),sQuery(id+"F0.wireOp",EDGE,"E211"),sQuery(id+"F0.wireOp",EDGE,"E212"),sQuery(id+"F0.wireOp",EDGE,"E248"),sQuery(id+"F0.wireOp",EDGE,"E249"),sQuery(id+"F0.wireOp",EDGE,"E250"),sQuery(id+"F0.wireOp",EDGE,"E251"),sQuery(id+"F0.wireOp",EDGE,"E252"),sQuery(id+"F0.wireOp",EDGE,"E253"),sQuery(id+"F0.wireOp",EDGE,"E254"),sQuery(id+"F0.wireOp",EDGE,"E273"),sQuery(id+"F0.wireOp",EDGE,"E274"),sQuery(id+"F0.wireOp",EDGE,"E275"),sQuery(id+"F0.wireOp",EDGE,"E276"),sQuery(id+"F0.wireOp",EDGE,"E277")])],"isStart":false});
            extrude(context, id + "F6", {"entities" : qUnion([Q0]), "depth" : 1.5 * mm});
        }
        {
            var Q0;
            Q0=makeQuery(id+"F2.opExtrude","SWEPT_BODY",BODY,{"disambiguationData":[OSD([sQuery(id+"F0.wireOp",EDGE,"E69"),sQuery(id+"F0.wireOp",EDGE,"E71"),sQuery(id+"F0.wireOp",EDGE,"E72"),sQuery(id+"F0.wireOp",EDGE,"E73"),sQuery(id+"F0.wireOp",EDGE,"E74"),sQuery(id+"F0.wireOp",EDGE,"E75"),sQuery(id+"F0.wireOp",EDGE,"E76"),sQuery(id+"F0.wireOp",EDGE,"E77"),sQuery(id+"F0.wireOp",EDGE,"E78"),sQuery(id+"F0.wireOp",EDGE,"E79"),sQuery(id+"F0.wireOp",EDGE,"E80"),sQuery(id+"F0.wireOp",EDGE,"E81"),sQuery(id+"F0.wireOp",EDGE,"E82"),sQuery(id+"F0.wireOp",EDGE,"E83"),sQuery(id+"F0.wireOp",EDGE,"E84"),sQuery(id+"F0.wireOp",EDGE,"E85"),sQuery(id+"F0.wireOp",EDGE,"E86"),sQuery(id+"F0.wireOp",EDGE,"E87"),sQuery(id+"F0.wireOp",EDGE,"E88"),sQuery(id+"F0.wireOp",EDGE,"E89"),sQuery(id+"F0.wireOp",EDGE,"E90"),sQuery(id+"F0.wireOp",EDGE,"E91"),sQuery(id+"F0.wireOp",EDGE,"E92"),sQuery(id+"F0.wireOp",EDGE,"E93"),sQuery(id+"F0.wireOp",EDGE,"E94"),sQuery(id+"F0.wireOp",EDGE,"E95"),sQuery(id+"F0.wireOp",EDGE,"E96"),sQuery(id+"F0.wireOp",EDGE,"E97"),sQuery(id+"F0.wireOp",EDGE,"E98"),sQuery(id+"F0.wireOp",EDGE,"E99"),sQuery(id+"F0.wireOp",EDGE,"E100"),sQuery(id+"F0.wireOp",EDGE,"E101"),sQuery(id+"F0.wireOp",EDGE,"E102"),sQuery(id+"F0.wireOp",EDGE,"E103"),sQuery(id+"F0.wireOp",EDGE,"E104"),sQuery(id+"F0.wireOp",EDGE,"E105"),sQuery(id+"F0.wireOp",EDGE,"E106"),sQuery(id+"F0.wireOp",EDGE,"E107"),sQuery(id+"F0.wireOp",EDGE,"E108"),sQuery(id+"F0.wireOp",EDGE,"E109"),sQuery(id+"F0.wireOp",EDGE,"E110"),sQuery(id+"F0.wireOp",EDGE,"E111"),sQuery(id+"F0.wireOp",EDGE,"E112"),sQuery(id+"F0.wireOp",EDGE,"E113"),sQuery(id+"F0.wireOp",EDGE,"E114"),sQuery(id+"F0.wireOp",EDGE,"E115"),sQuery(id+"F0.wireOp",EDGE,"E116"),sQuery(id+"F0.wireOp",EDGE,"E117"),sQuery(id+"F0.wireOp",EDGE,"E118"),sQuery(id+"F0.wireOp",EDGE,"E119"),sQuery(id+"F0.wireOp",EDGE,"E120"),sQuery(id+"F0.wireOp",EDGE,"E121"),sQuery(id+"F0.wireOp",EDGE,"E122"),sQuery(id+"F0.wireOp",EDGE,"E123"),sQuery(id+"F0.wireOp",EDGE,"E124"),sQuery(id+"F0.wireOp",EDGE,"E125"),sQuery(id+"F0.wireOp",EDGE,"E126"),sQuery(id+"F0.wireOp",EDGE,"E127"),sQuery(id+"F0.wireOp",EDGE,"E128"),sQuery(id+"F0.wireOp",EDGE,"E129"),sQuery(id+"F0.wireOp",EDGE,"E130"),sQuery(id+"F0.wireOp",EDGE,"E131"),sQuery(id+"F0.wireOp",EDGE,"E132"),sQuery(id+"F0.wireOp",EDGE,"E133"),sQuery(id+"F0.wireOp",EDGE,"E134"),sQuery(id+"F0.wireOp",EDGE,"E135"),sQuery(id+"F0.wireOp",EDGE,"E136"),sQuery(id+"F0.wireOp",EDGE,"E204"),sQuery(id+"F0.wireOp",EDGE,"E277"),sQuery(id+"F0.wireOp",EDGE,"E278")])]});
            transform(context, id + "F7", {"entities" : qUnion([Q0]), "transformType" : TransformType.TRANSLATION_3D, "dx" : 0 * mm, "dy" : 0 * mm, "dz" : 5 * mm, "makeCopy" : false});
        }
        {
            var Q0;
            Q0=makeQuery(id+"F3.opExtrude","SWEPT_BODY",BODY,{"disambiguationData":[OSD([sQuery(id+"F0.wireOp",EDGE,"E0"),sQuery(id+"F0.wireOp",EDGE,"E2"),sQuery(id+"F0.wireOp",EDGE,"E3"),sQuery(id+"F0.wireOp",EDGE,"E4"),sQuery(id+"F0.wireOp",EDGE,"E5"),sQuery(id+"F0.wireOp",EDGE,"E6"),sQuery(id+"F0.wireOp",EDGE,"E7"),sQuery(id+"F0.wireOp",EDGE,"E8"),sQuery(id+"F0.wireOp",EDGE,"E9"),sQuery(id+"F0.wireOp",EDGE,"E10"),sQuery(id+"F0.wireOp",EDGE,"E11"),sQuery(id+"F0.wireOp",EDGE,"E12"),sQuery(id+"F0.wireOp",EDGE,"E13"),sQuery(id+"F0.wireOp",EDGE,"E14"),sQuery(id+"F0.wireOp",EDGE,"E15"),sQuery(id+"F0.wireOp",EDGE,"E16"),sQuery(id+"F0.wireOp",EDGE,"E17"),sQuery(id+"F0.wireOp",EDGE,"E18"),sQuery(id+"F0.wireOp",EDGE,"E19"),sQuery(id+"F0.wireOp",EDGE,"E20"),sQuery(id+"F0.wireOp",EDGE,"E21"),sQuery(id+"F0.wireOp",EDGE,"E22"),sQuery(id+"F0.wireOp",EDGE,"E23"),sQuery(id+"F0.wireOp",EDGE,"E24"),sQuery(id+"F0.wireOp",EDGE,"E25"),sQuery(id+"F0.wireOp",EDGE,"E26"),sQuery(id+"F0.wireOp",EDGE,"E27"),sQuery(id+"F0.wireOp",EDGE,"E28"),sQuery(id+"F0.wireOp",EDGE,"E29"),sQuery(id+"F0.wireOp",EDGE,"E30"),sQuery(id+"F0.wireOp",EDGE,"E31"),sQuery(id+"F0.wireOp",EDGE,"E32"),sQuery(id+"F0.wireOp",EDGE,"E33"),sQuery(id+"F0.wireOp",EDGE,"E34"),sQuery(id+"F0.wireOp",EDGE,"E35"),sQuery(id+"F0.wireOp",EDGE,"E36"),sQuery(id+"F0.wireOp",EDGE,"E37"),sQuery(id+"F0.wireOp",EDGE,"E38"),sQuery(id+"F0.wireOp",EDGE,"E39"),sQuery(id+"F0.wireOp",EDGE,"E40"),sQuery(id+"F0.wireOp",EDGE,"E41"),sQuery(id+"F0.wireOp",EDGE,"E42"),sQuery(id+"F0.wireOp",EDGE,"E43"),sQuery(id+"F0.wireOp",EDGE,"E44"),sQuery(id+"F0.wireOp",EDGE,"E45"),sQuery(id+"F0.wireOp",EDGE,"E46"),sQuery(id+"F0.wireOp",EDGE,"E47"),sQuery(id+"F0.wireOp",EDGE,"E48"),sQuery(id+"F0.wireOp",EDGE,"E49"),sQuery(id+"F0.wireOp",EDGE,"E50"),sQuery(id+"F0.wireOp",EDGE,"E51"),sQuery(id+"F0.wireOp",EDGE,"E52"),sQuery(id+"F0.wireOp",EDGE,"E53"),sQuery(id+"F0.wireOp",EDGE,"E54"),sQuery(id+"F0.wireOp",EDGE,"E55"),sQuery(id+"F0.wireOp",EDGE,"E56"),sQuery(id+"F0.wireOp",EDGE,"E57"),sQuery(id+"F0.wireOp",EDGE,"E58"),sQuery(id+"F0.wireOp",EDGE,"E59"),sQuery(id+"F0.wireOp",EDGE,"E60"),sQuery(id+"F0.wireOp",EDGE,"E61"),sQuery(id+"F0.wireOp",EDGE,"E62"),sQuery(id+"F0.wireOp",EDGE,"E63"),sQuery(id+"F0.wireOp",EDGE,"E64"),sQuery(id+"F0.wireOp",EDGE,"E65"),sQuery(id+"F0.wireOp",EDGE,"E66"),sQuery(id+"F0.wireOp",EDGE,"E67"),sQuery(id+"F0.wireOp",EDGE,"E274"),sQuery(id+"F0.wireOp",EDGE,"E278"),sQuery(id+"F0.wireOp",EDGE,"E279")])]});
            transform(context, id + "F8", {"entities" : qUnion([Q0]), "transformType" : TransformType.TRANSLATION_3D, "dx" : 0 * mm, "dy" : 0 * mm, "dz" : 5 * mm, "makeCopy" : false});
        }
        {
            var Q0;
            Q0=makeQuery(id+"F1.opExtrude","SWEPT_BODY",BODY,{"disambiguationData":[OSD([sQuery(id+"F0.wireOp",EDGE,"E204"),sQuery(id+"F0.wireOp",EDGE,"E206"),sQuery(id+"F0.wireOp",EDGE,"E207"),sQuery(id+"F0.wireOp",EDGE,"E208"),sQuery(id+"F0.wireOp",EDGE,"E209"),sQuery(id+"F0.wireOp",EDGE,"E210"),sQuery(id+"F0.wireOp",EDGE,"E211"),sQuery(id+"F0.wireOp",EDGE,"E212"),sQuery(id+"F0.wireOp",EDGE,"E213"),sQuery(id+"F0.wireOp",EDGE,"E214"),sQuery(id+"F0.wireOp",EDGE,"E215"),sQuery(id+"F0.wireOp",EDGE,"E216"),sQuery(id+"F0.wireOp",EDGE,"E217"),sQuery(id+"F0.wireOp",EDGE,"E218"),sQuery(id+"F0.wireOp",EDGE,"E219"),sQuery(id+"F0.wireOp",EDGE,"E220"),sQuery(id+"F0.wireOp",EDGE,"E221"),sQuery(id+"F0.wireOp",EDGE,"E222"),sQuery(id+"F0.wireOp",EDGE,"E223"),sQuery(id+"F0.wireOp",EDGE,"E224"),sQuery(id+"F0.wireOp",EDGE,"E225"),sQuery(id+"F0.wireOp",EDGE,"E226"),sQuery(id+"F0.wireOp",EDGE,"E227"),sQuery(id+"F0.wireOp",EDGE,"E228"),sQuery(id+"F0.wireOp",EDGE,"E229"),sQuery(id+"F0.wireOp",EDGE,"E230"),sQuery(id+"F0.wireOp",EDGE,"E231"),sQuery(id+"F0.wireOp",EDGE,"E232"),sQuery(id+"F0.wireOp",EDGE,"E233"),sQuery(id+"F0.wireOp",EDGE,"E234"),sQuery(id+"F0.wireOp",EDGE,"E235"),sQuery(id+"F0.wireOp",EDGE,"E236"),sQuery(id+"F0.wireOp",EDGE,"E237"),sQuery(id+"F0.wireOp",EDGE,"E238"),sQuery(id+"F0.wireOp",EDGE,"E239"),sQuery(id+"F0.wireOp",EDGE,"E240"),sQuery(id+"F0.wireOp",EDGE,"E241"),sQuery(id+"F0.wireOp",EDGE,"E242"),sQuery(id+"F0.wireOp",EDGE,"E243"),sQuery(id+"F0.wireOp",EDGE,"E244"),sQuery(id+"F0.wireOp",EDGE,"E245"),sQuery(id+"F0.wireOp",EDGE,"E246"),sQuery(id+"F0.wireOp",EDGE,"E247"),sQuery(id+"F0.wireOp",EDGE,"E248"),sQuery(id+"F0.wireOp",EDGE,"E249"),sQuery(id+"F0.wireOp",EDGE,"E250"),sQuery(id+"F0.wireOp",EDGE,"E251"),sQuery(id+"F0.wireOp",EDGE,"E252"),sQuery(id+"F0.wireOp",EDGE,"E253"),sQuery(id+"F0.wireOp",EDGE,"E254"),sQuery(id+"F0.wireOp",EDGE,"E255"),sQuery(id+"F0.wireOp",EDGE,"E256"),sQuery(id+"F0.wireOp",EDGE,"E257"),sQuery(id+"F0.wireOp",EDGE,"E258"),sQuery(id+"F0.wireOp",EDGE,"E259"),sQuery(id+"F0.wireOp",EDGE,"E260"),sQuery(id+"F0.wireOp",EDGE,"E261"),sQuery(id+"F0.wireOp",EDGE,"E262"),sQuery(id+"F0.wireOp",EDGE,"E263"),sQuery(id+"F0.wireOp",EDGE,"E264"),sQuery(id+"F0.wireOp",EDGE,"E265"),sQuery(id+"F0.wireOp",EDGE,"E266"),sQuery(id+"F0.wireOp",EDGE,"E267"),sQuery(id+"F0.wireOp",EDGE,"E268"),sQuery(id+"F0.wireOp",EDGE,"E269"),sQuery(id+"F0.wireOp",EDGE,"E270"),sQuery(id+"F0.wireOp",EDGE,"E271"),sQuery(id+"F0.wireOp",EDGE,"E272"),sQuery(id+"F0.wireOp",EDGE,"E273"),sQuery(id+"F0.wireOp",EDGE,"E276")])]});
            transform(context, id + "F9", {"entities" : qUnion([Q0]), "transformType" : TransformType.TRANSLATION_3D, "dx" : 0 * mm, "dy" : 0 * mm, "dz" : 5 * mm, "makeCopy" : false});
        }
        {
            var Q0;
            Q0=makeQuery(id+"F4.opExtrude","SWEPT_BODY",BODY,{"disambiguationData":[OSD([sQuery(id+"F0.wireOp",EDGE,"E68"),sQuery(id+"F0.wireOp",EDGE,"E138"),sQuery(id+"F0.wireOp",EDGE,"E139"),sQuery(id+"F0.wireOp",EDGE,"E140"),sQuery(id+"F0.wireOp",EDGE,"E141"),sQuery(id+"F0.wireOp",EDGE,"E142"),sQuery(id+"F0.wireOp",EDGE,"E143"),sQuery(id+"F0.wireOp",EDGE,"E144"),sQuery(id+"F0.wireOp",EDGE,"E145"),sQuery(id+"F0.wireOp",EDGE,"E146"),sQuery(id+"F0.wireOp",EDGE,"E147"),sQuery(id+"F0.wireOp",EDGE,"E148"),sQuery(id+"F0.wireOp",EDGE,"E149"),sQuery(id+"F0.wireOp",EDGE,"E150"),sQuery(id+"F0.wireOp",EDGE,"E151"),sQuery(id+"F0.wireOp",EDGE,"E152"),sQuery(id+"F0.wireOp",EDGE,"E153"),sQuery(id+"F0.wireOp",EDGE,"E154"),sQuery(id+"F0.wireOp",EDGE,"E155"),sQuery(id+"F0.wireOp",EDGE,"E156"),sQuery(id+"F0.wireOp",EDGE,"E157"),sQuery(id+"F0.wireOp",EDGE,"E158"),sQuery(id+"F0.wireOp",EDGE,"E159"),sQuery(id+"F0.wireOp",EDGE,"E160"),sQuery(id+"F0.wireOp",EDGE,"E161"),sQuery(id+"F0.wireOp",EDGE,"E162"),sQuery(id+"F0.wireOp",EDGE,"E163"),sQuery(id+"F0.wireOp",EDGE,"E164"),sQuery(id+"F0.wireOp",EDGE,"E165"),sQuery(id+"F0.wireOp",EDGE,"E166"),sQuery(id+"F0.wireOp",EDGE,"E167"),sQuery(id+"F0.wireOp",EDGE,"E168"),sQuery(id+"F0.wireOp",EDGE,"E169"),sQuery(id+"F0.wireOp",EDGE,"E170"),sQuery(id+"F0.wireOp",EDGE,"E171"),sQuery(id+"F0.wireOp",EDGE,"E172"),sQuery(id+"F0.wireOp",EDGE,"E173"),sQuery(id+"F0.wireOp",EDGE,"E174"),sQuery(id+"F0.wireOp",EDGE,"E175"),sQuery(id+"F0.wireOp",EDGE,"E176"),sQuery(id+"F0.wireOp",EDGE,"E177"),sQuery(id+"F0.wireOp",EDGE,"E178"),sQuery(id+"F0.wireOp",EDGE,"E179"),sQuery(id+"F0.wireOp",EDGE,"E180"),sQuery(id+"F0.wireOp",EDGE,"E181"),sQuery(id+"F0.wireOp",EDGE,"E182"),sQuery(id+"F0.wireOp",EDGE,"E183"),sQuery(id+"F0.wireOp",EDGE,"E184"),sQuery(id+"F0.wireOp",EDGE,"E185"),sQuery(id+"F0.wireOp",EDGE,"E186"),sQuery(id+"F0.wireOp",EDGE,"E187"),sQuery(id+"F0.wireOp",EDGE,"E188"),sQuery(id+"F0.wireOp",EDGE,"E189"),sQuery(id+"F0.wireOp",EDGE,"E190"),sQuery(id+"F0.wireOp",EDGE,"E191"),sQuery(id+"F0.wireOp",EDGE,"E192"),sQuery(id+"F0.wireOp",EDGE,"E193"),sQuery(id+"F0.wireOp",EDGE,"E194"),sQuery(id+"F0.wireOp",EDGE,"E195"),sQuery(id+"F0.wireOp",EDGE,"E196"),sQuery(id+"F0.wireOp",EDGE,"E197"),sQuery(id+"F0.wireOp",EDGE,"E198"),sQuery(id+"F0.wireOp",EDGE,"E199"),sQuery(id+"F0.wireOp",EDGE,"E200"),sQuery(id+"F0.wireOp",EDGE,"E201"),sQuery(id+"F0.wireOp",EDGE,"E202"),sQuery(id+"F0.wireOp",EDGE,"E203"),sQuery(id+"F0.wireOp",EDGE,"E272"),sQuery(id+"F0.wireOp",EDGE,"E275"),sQuery(id+"F0.wireOp",EDGE,"E279")])]});
            transform(context, id + "F10", {"entities" : qUnion([Q0]), "transformType" : TransformType.TRANSLATION_3D, "dx" : 0 * mm, "dy" : 0 * mm, "dz" : 5 * mm, "makeCopy" : false});
        }
        {
            var Q0;
            Q0=makeQuery(id+"F5.opExtrude","SWEPT_BODY",BODY,{"disambiguationData":[OSD([sQuery(id+"F0.wireOp",EDGE,"E0"),sQuery(id+"F0.wireOp",EDGE,"E1"),sQuery(id+"F0.wireOp",EDGE,"E2"),sQuery(id+"F0.wireOp",EDGE,"E3"),sQuery(id+"F0.wireOp",EDGE,"E4"),sQuery(id+"F0.wireOp",EDGE,"E5"),sQuery(id+"F0.wireOp",EDGE,"E6"),sQuery(id+"F0.wireOp",EDGE,"E7"),sQuery(id+"F0.wireOp",EDGE,"E8"),sQuery(id+"F0.wireOp",EDGE,"E44"),sQuery(id+"F0.wireOp",EDGE,"E45"),sQuery(id+"F0.wireOp",EDGE,"E46"),sQuery(id+"F0.wireOp",EDGE,"E47"),sQuery(id+"F0.wireOp",EDGE,"E48"),sQuery(id+"F0.wireOp",EDGE,"E49"),sQuery(id+"F0.wireOp",EDGE,"E50"),sQuery(id+"F0.wireOp",EDGE,"E68"),sQuery(id+"F0.wireOp",EDGE,"E69"),sQuery(id+"F0.wireOp",EDGE,"E70"),sQuery(id+"F0.wireOp",EDGE,"E71"),sQuery(id+"F0.wireOp",EDGE,"E72"),sQuery(id+"F0.wireOp",EDGE,"E73"),sQuery(id+"F0.wireOp",EDGE,"E74"),sQuery(id+"F0.wireOp",EDGE,"E75"),sQuery(id+"F0.wireOp",EDGE,"E76"),sQuery(id+"F0.wireOp",EDGE,"E77"),sQuery(id+"F0.wireOp",EDGE,"E113"),sQuery(id+"F0.wireOp",EDGE,"E114"),sQuery(id+"F0.wireOp",EDGE,"E115"),sQuery(id+"F0.wireOp",EDGE,"E116"),sQuery(id+"F0.wireOp",EDGE,"E117"),sQuery(id+"F0.wireOp",EDGE,"E118"),sQuery(id+"F0.wireOp",EDGE,"E119"),sQuery(id+"F0.wireOp",EDGE,"E137"),sQuery(id+"F0.wireOp",EDGE,"E138"),sQuery(id+"F0.wireOp",EDGE,"E139"),sQuery(id+"F0.wireOp",EDGE,"E140"),sQuery(id+"F0.wireOp",EDGE,"E141"),sQuery(id+"F0.wireOp",EDGE,"E142"),sQuery(id+"F0.wireOp",EDGE,"E143"),sQuery(id+"F0.wireOp",EDGE,"E144"),sQuery(id+"F0.wireOp",EDGE,"E180"),sQuery(id+"F0.wireOp",EDGE,"E181"),sQuery(id+"F0.wireOp",EDGE,"E182"),sQuery(id+"F0.wireOp",EDGE,"E183"),sQuery(id+"F0.wireOp",EDGE,"E184"),sQuery(id+"F0.wireOp",EDGE,"E185"),sQuery(id+"F0.wireOp",EDGE,"E186"),sQuery(id+"F0.wireOp",EDGE,"E204"),sQuery(id+"F0.wireOp",EDGE,"E205"),sQuery(id+"F0.wireOp",EDGE,"E206"),sQuery(id+"F0.wireOp",EDGE,"E207"),sQuery(id+"F0.wireOp",EDGE,"E208"),sQuery(id+"F0.wireOp",EDGE,"E209"),sQuery(id+"F0.wireOp",EDGE,"E210"),sQuery(id+"F0.wireOp",EDGE,"E211"),sQuery(id+"F0.wireOp",EDGE,"E212"),sQuery(id+"F0.wireOp",EDGE,"E248"),sQuery(id+"F0.wireOp",EDGE,"E249"),sQuery(id+"F0.wireOp",EDGE,"E250"),sQuery(id+"F0.wireOp",EDGE,"E251"),sQuery(id+"F0.wireOp",EDGE,"E252"),sQuery(id+"F0.wireOp",EDGE,"E253"),sQuery(id+"F0.wireOp",EDGE,"E254"),sQuery(id+"F0.wireOp",EDGE,"E273"),sQuery(id+"F0.wireOp",EDGE,"E274"),sQuery(id+"F0.wireOp",EDGE,"E275"),sQuery(id+"F0.wireOp",EDGE,"E276"),sQuery(id+"F0.wireOp",EDGE,"E277")])]});
            transform(context, id + "F11", {"entities" : qUnion([Q0]), "transformType" : TransformType.TRANSLATION_3D, "dx" : 0 * mm, "dy" : 0 * mm, "dz" : 9 * mm, "makeCopy" : false});
        }
        {
            var Q0;
            Q0=makeQuery(id+"F6.opExtrude","SWEPT_BODY",BODY,{"disambiguationData":[OSD([sQuery(id+"F0.wireOp",EDGE,"E0"),sQuery(id+"F0.wireOp",EDGE,"E1"),sQuery(id+"F0.wireOp",EDGE,"E2"),sQuery(id+"F0.wireOp",EDGE,"E3"),sQuery(id+"F0.wireOp",EDGE,"E4"),sQuery(id+"F0.wireOp",EDGE,"E5"),sQuery(id+"F0.wireOp",EDGE,"E6"),sQuery(id+"F0.wireOp",EDGE,"E7"),sQuery(id+"F0.wireOp",EDGE,"E8"),sQuery(id+"F0.wireOp",EDGE,"E44"),sQuery(id+"F0.wireOp",EDGE,"E45"),sQuery(id+"F0.wireOp",EDGE,"E46"),sQuery(id+"F0.wireOp",EDGE,"E47"),sQuery(id+"F0.wireOp",EDGE,"E48"),sQuery(id+"F0.wireOp",EDGE,"E49"),sQuery(id+"F0.wireOp",EDGE,"E50"),sQuery(id+"F0.wireOp",EDGE,"E68"),sQuery(id+"F0.wireOp",EDGE,"E69"),sQuery(id+"F0.wireOp",EDGE,"E70"),sQuery(id+"F0.wireOp",EDGE,"E71"),sQuery(id+"F0.wireOp",EDGE,"E72"),sQuery(id+"F0.wireOp",EDGE,"E73"),sQuery(id+"F0.wireOp",EDGE,"E74"),sQuery(id+"F0.wireOp",EDGE,"E75"),sQuery(id+"F0.wireOp",EDGE,"E76"),sQuery(id+"F0.wireOp",EDGE,"E77"),sQuery(id+"F0.wireOp",EDGE,"E113"),sQuery(id+"F0.wireOp",EDGE,"E114"),sQuery(id+"F0.wireOp",EDGE,"E115"),sQuery(id+"F0.wireOp",EDGE,"E116"),sQuery(id+"F0.wireOp",EDGE,"E117"),sQuery(id+"F0.wireOp",EDGE,"E118"),sQuery(id+"F0.wireOp",EDGE,"E119"),sQuery(id+"F0.wireOp",EDGE,"E137"),sQuery(id+"F0.wireOp",EDGE,"E138"),sQuery(id+"F0.wireOp",EDGE,"E139"),sQuery(id+"F0.wireOp",EDGE,"E140"),sQuery(id+"F0.wireOp",EDGE,"E141"),sQuery(id+"F0.wireOp",EDGE,"E142"),sQuery(id+"F0.wireOp",EDGE,"E143"),sQuery(id+"F0.wireOp",EDGE,"E144"),sQuery(id+"F0.wireOp",EDGE,"E180"),sQuery(id+"F0.wireOp",EDGE,"E181"),sQuery(id+"F0.wireOp",EDGE,"E182"),sQuery(id+"F0.wireOp",EDGE,"E183"),sQuery(id+"F0.wireOp",EDGE,"E184"),sQuery(id+"F0.wireOp",EDGE,"E185"),sQuery(id+"F0.wireOp",EDGE,"E186"),sQuery(id+"F0.wireOp",EDGE,"E204"),sQuery(id+"F0.wireOp",EDGE,"E205"),sQuery(id+"F0.wireOp",EDGE,"E206"),sQuery(id+"F0.wireOp",EDGE,"E207"),sQuery(id+"F0.wireOp",EDGE,"E208"),sQuery(id+"F0.wireOp",EDGE,"E209"),sQuery(id+"F0.wireOp",EDGE,"E210"),sQuery(id+"F0.wireOp",EDGE,"E211"),sQuery(id+"F0.wireOp",EDGE,"E212"),sQuery(id+"F0.wireOp",EDGE,"E248"),sQuery(id+"F0.wireOp",EDGE,"E249"),sQuery(id+"F0.wireOp",EDGE,"E250"),sQuery(id+"F0.wireOp",EDGE,"E251"),sQuery(id+"F0.wireOp",EDGE,"E252"),sQuery(id+"F0.wireOp",EDGE,"E253"),sQuery(id+"F0.wireOp",EDGE,"E254"),sQuery(id+"F0.wireOp",EDGE,"E273"),sQuery(id+"F0.wireOp",EDGE,"E274"),sQuery(id+"F0.wireOp",EDGE,"E275"),sQuery(id+"F0.wireOp",EDGE,"E276"),sQuery(id+"F0.wireOp",EDGE,"E277")])]});
            transform(context, id + "F12", {"entities" : qUnion([Q0]), "transformType" : TransformType.TRANSLATION_3D, "dx" : 0 * mm, "dy" : 0 * mm, "dz" : 2 * mm, "makeCopy" : false});
        }
        {
            var Q0;
            Q0=makeQuery(id+"F0.imprint","IMPRINT",FACE,{"disambiguationData":[TD([[makeQuery(id+"F0.imprint","IMPRINT",EDGE,{"derivedFrom":sQuery(id+"F0.wireOp",EDGE,"E68")}),1.0]])]});
            var Q1;
            Q1=makeQuery(id+"F0.imprint","IMPRINT",FACE,{"disambiguationData":[TD([[makeQuery(id+"F0.imprint","IMPRINT",EDGE,{"derivedFrom":sQuery(id+"F0.wireOp",EDGE,"E275")}),-1.0]])]});
            var Q2;
            Q2=makeQuery(id+"F0.imprint","IMPRINT",FACE,{"disambiguationData":[TD([[makeQuery(id+"F0.imprint","IMPRINT",EDGE,{"derivedFrom":sQuery(id+"F0.wireOp",EDGE,"E69")}),1.0]])]});
            var Q3;
            Q3=makeQuery(id+"F0.imprint","IMPRINT",FACE,{"disambiguationData":[TD([[makeQuery(id+"F0.imprint","IMPRINT",EDGE,{"derivedFrom":sQuery(id+"F0.wireOp",EDGE,"E277")}),-1.0]])]});
            var Q4;
            Q4=makeQuery(id+"F0.imprint","IMPRINT",FACE,{"disambiguationData":[TD([[makeQuery(id+"F0.imprint","IMPRINT",EDGE,{"derivedFrom":sQuery(id+"F0.wireOp",EDGE,"E0")}),1.0]])]});
            var Q5;
            Q5=makeQuery(id+"F0.imprint","IMPRINT",FACE,{"disambiguationData":[TD([[makeQuery(id+"F0.imprint","IMPRINT",EDGE,{"derivedFrom":sQuery(id+"F0.wireOp",EDGE,"E274")}),-1.0]])]});
            var Q6;
            {var subQ1=sQuery(id+"F0.wireOp",EDGE,"E205");Q6=makeQuery(id+"F0.imprint","IMPRINT",FACE,{"disambiguationData":[TD([[makeQuery(id+"F0.imprint","IMPRINT",EDGE,{"derivedFrom":subQ1}),1.0]])]});}
            var Q7;
            Q7=makeQuery(id+"F0.imprint","IMPRINT",FACE,{"disambiguationData":[TD([[makeQuery(id+"F0.imprint","IMPRINT",EDGE,{"derivedFrom":sQuery(id+"F0.wireOp",EDGE,"E276")}),-1.0]])]});
            extrude(context, id + "F13", {"entities" : qUnion([Q0, Q1, Q2, Q3, Q4, Q5, Q6, Q7]), "depth" : 1.5 * mm});
        }
        {
            var Q0;
            Q0=makeQuery(id+"F13.opExtrude","SWEPT_BODY",BODY,{"disambiguationData":[OSD([sQuery(id+"F0.wireOp",EDGE,"E0"),sQuery(id+"F0.wireOp",EDGE,"E1"),sQuery(id+"F0.wireOp",EDGE,"E2"),sQuery(id+"F0.wireOp",EDGE,"E3"),sQuery(id+"F0.wireOp",EDGE,"E4"),sQuery(id+"F0.wireOp",EDGE,"E5"),sQuery(id+"F0.wireOp",EDGE,"E6"),sQuery(id+"F0.wireOp",EDGE,"E7"),sQuery(id+"F0.wireOp",EDGE,"E8"),sQuery(id+"F0.wireOp",EDGE,"E44"),sQuery(id+"F0.wireOp",EDGE,"E45"),sQuery(id+"F0.wireOp",EDGE,"E46"),sQuery(id+"F0.wireOp",EDGE,"E47"),sQuery(id+"F0.wireOp",EDGE,"E48"),sQuery(id+"F0.wireOp",EDGE,"E49"),sQuery(id+"F0.wireOp",EDGE,"E50"),sQuery(id+"F0.wireOp",EDGE,"E68"),sQuery(id+"F0.wireOp",EDGE,"E69"),sQuery(id+"F0.wireOp",EDGE,"E70"),sQuery(id+"F0.wireOp",EDGE,"E71"),sQuery(id+"F0.wireOp",EDGE,"E72"),sQuery(id+"F0.wireOp",EDGE,"E73"),sQuery(id+"F0.wireOp",EDGE,"E74"),sQuery(id+"F0.wireOp",EDGE,"E75"),sQuery(id+"F0.wireOp",EDGE,"E76"),sQuery(id+"F0.wireOp",EDGE,"E77"),sQuery(id+"F0.wireOp",EDGE,"E113"),sQuery(id+"F0.wireOp",EDGE,"E114"),sQuery(id+"F0.wireOp",EDGE,"E115"),sQuery(id+"F0.wireOp",EDGE,"E116"),sQuery(id+"F0.wireOp",EDGE,"E117"),sQuery(id+"F0.wireOp",EDGE,"E118"),sQuery(id+"F0.wireOp",EDGE,"E119"),sQuery(id+"F0.wireOp",EDGE,"E137"),sQuery(id+"F0.wireOp",EDGE,"E138"),sQuery(id+"F0.wireOp",EDGE,"E139"),sQuery(id+"F0.wireOp",EDGE,"E140"),sQuery(id+"F0.wireOp",EDGE,"E141"),sQuery(id+"F0.wireOp",EDGE,"E142"),sQuery(id+"F0.wireOp",EDGE,"E143"),sQuery(id+"F0.wireOp",EDGE,"E144"),sQuery(id+"F0.wireOp",EDGE,"E180"),sQuery(id+"F0.wireOp",EDGE,"E181"),sQuery(id+"F0.wireOp",EDGE,"E182"),sQuery(id+"F0.wireOp",EDGE,"E183"),sQuery(id+"F0.wireOp",EDGE,"E184"),sQuery(id+"F0.wireOp",EDGE,"E185"),sQuery(id+"F0.wireOp",EDGE,"E186"),sQuery(id+"F0.wireOp",EDGE,"E204"),sQuery(id+"F0.wireOp",EDGE,"E205"),sQuery(id+"F0.wireOp",EDGE,"E206"),sQuery(id+"F0.wireOp",EDGE,"E207"),sQuery(id+"F0.wireOp",EDGE,"E208"),sQuery(id+"F0.wireOp",EDGE,"E209"),sQuery(id+"F0.wireOp",EDGE,"E210"),sQuery(id+"F0.wireOp",EDGE,"E211"),sQuery(id+"F0.wireOp",EDGE,"E212"),sQuery(id+"F0.wireOp",EDGE,"E248"),sQuery(id+"F0.wireOp",EDGE,"E249"),sQuery(id+"F0.wireOp",EDGE,"E250"),sQuery(id+"F0.wireOp",EDGE,"E251"),sQuery(id+"F0.wireOp",EDGE,"E252"),sQuery(id+"F0.wireOp",EDGE,"E253"),sQuery(id+"F0.wireOp",EDGE,"E254"),sQuery(id+"F0.wireOp",EDGE,"E273")])]});
            transform(context, id + "F14", {"entities" : qUnion([Q0]), "transformType" : TransformType.TRANSLATION_3D, "dx" : 0 * mm, "dy" : 0 * mm, "dz" : 40.5 * mm, "makeCopy" : false});
        }
        {
            var Q0;
            Q0=makeQuery(id+"F0.imprint","IMPRINT",FACE,{"disambiguationData":[TD([[makeQuery(id+"F0.imprint","IMPRINT",EDGE,{"derivedFrom":sQuery(id+"F0.wireOp",EDGE,"E273")}),-1.0]])]});
            var Q1;
            Q1=makeQuery(id+"F0.imprint","IMPRINT",FACE,{"disambiguationData":[TD([[makeQuery(id+"F0.imprint","IMPRINT",EDGE,{"derivedFrom":sQuery(id+"F0.wireOp",EDGE,"E69")}),-1.0]])]});
            var Q2;
            Q2=makeQuery(id+"F0.imprint","IMPRINT",FACE,{"disambiguationData":[TD([[makeQuery(id+"F0.imprint","IMPRINT",EDGE,{"derivedFrom":sQuery(id+"F0.wireOp",EDGE,"E0")}),-1.0]])]});
            var Q3;
            Q3=makeQuery(id+"F0.imprint","IMPRINT",FACE,{"disambiguationData":[TD([[makeQuery(id+"F0.imprint","IMPRINT",EDGE,{"derivedFrom":sQuery(id+"F0.wireOp",EDGE,"E68")}),-1.0]])]});
            extrude(context, id + "F15", {"entities" : qUnion([Q0, Q1, Q2, Q3]), "depth" : 30 * mm});
        }
        {
            var Q0;
            Q0=makeQuery(id+"F15.opExtrude","SWEPT_BODY",BODY,{"disambiguationData":[OSD([sQuery(id+"F0.wireOp",EDGE,"E68")])]});
            var Q1;
            Q1=makeQuery(id+"F15.opExtrude","SWEPT_BODY",BODY,{"disambiguationData":[OSD([sQuery(id+"F0.wireOp",EDGE,"E0")])]});
            var Q2;
            Q2=makeQuery(id+"F15.opExtrude","SWEPT_BODY",BODY,{"disambiguationData":[OSD([sQuery(id+"F0.wireOp",EDGE,"E69")])]});
            var Q3;
            Q3=makeQuery(id+"F15.opExtrude","SWEPT_BODY",BODY,{"disambiguationData":[OSD([sQuery(id+"F0.wireOp",EDGE,"E273")])]});
            transform(context, id + "F16", {"entities" : qUnion([Q0, Q1, Q2, Q3]), "transformType" : TransformType.TRANSLATION_3D, "dx" : 0 * mm, "dy" : 0 * mm, "dz" : 10.5 * mm, "makeCopy" : false});
        }
        {
            var Q0;
            Q0=makeQuery(id+"F1.opExtrude","SWEPT_BODY",BODY,{"disambiguationData":[OSD([sQuery(id+"F0.wireOp",EDGE,"E204"),sQuery(id+"F0.wireOp",EDGE,"E206"),sQuery(id+"F0.wireOp",EDGE,"E207"),sQuery(id+"F0.wireOp",EDGE,"E208"),sQuery(id+"F0.wireOp",EDGE,"E209"),sQuery(id+"F0.wireOp",EDGE,"E210"),sQuery(id+"F0.wireOp",EDGE,"E211"),sQuery(id+"F0.wireOp",EDGE,"E212"),sQuery(id+"F0.wireOp",EDGE,"E213"),sQuery(id+"F0.wireOp",EDGE,"E214"),sQuery(id+"F0.wireOp",EDGE,"E215"),sQuery(id+"F0.wireOp",EDGE,"E216"),sQuery(id+"F0.wireOp",EDGE,"E217"),sQuery(id+"F0.wireOp",EDGE,"E218"),sQuery(id+"F0.wireOp",EDGE,"E219"),sQuery(id+"F0.wireOp",EDGE,"E220"),sQuery(id+"F0.wireOp",EDGE,"E221"),sQuery(id+"F0.wireOp",EDGE,"E222"),sQuery(id+"F0.wireOp",EDGE,"E223"),sQuery(id+"F0.wireOp",EDGE,"E224"),sQuery(id+"F0.wireOp",EDGE,"E225"),sQuery(id+"F0.wireOp",EDGE,"E226"),sQuery(id+"F0.wireOp",EDGE,"E227"),sQuery(id+"F0.wireOp",EDGE,"E228"),sQuery(id+"F0.wireOp",EDGE,"E229"),sQuery(id+"F0.wireOp",EDGE,"E230"),sQuery(id+"F0.wireOp",EDGE,"E231"),sQuery(id+"F0.wireOp",EDGE,"E232"),sQuery(id+"F0.wireOp",EDGE,"E233"),sQuery(id+"F0.wireOp",EDGE,"E234"),sQuery(id+"F0.wireOp",EDGE,"E235"),sQuery(id+"F0.wireOp",EDGE,"E236"),sQuery(id+"F0.wireOp",EDGE,"E237"),sQuery(id+"F0.wireOp",EDGE,"E238"),sQuery(id+"F0.wireOp",EDGE,"E239"),sQuery(id+"F0.wireOp",EDGE,"E240"),sQuery(id+"F0.wireOp",EDGE,"E241"),sQuery(id+"F0.wireOp",EDGE,"E242"),sQuery(id+"F0.wireOp",EDGE,"E243"),sQuery(id+"F0.wireOp",EDGE,"E244"),sQuery(id+"F0.wireOp",EDGE,"E245"),sQuery(id+"F0.wireOp",EDGE,"E246"),sQuery(id+"F0.wireOp",EDGE,"E247"),sQuery(id+"F0.wireOp",EDGE,"E248"),sQuery(id+"F0.wireOp",EDGE,"E249"),sQuery(id+"F0.wireOp",EDGE,"E250"),sQuery(id+"F0.wireOp",EDGE,"E251"),sQuery(id+"F0.wireOp",EDGE,"E252"),sQuery(id+"F0.wireOp",EDGE,"E253"),sQuery(id+"F0.wireOp",EDGE,"E254"),sQuery(id+"F0.wireOp",EDGE,"E255"),sQuery(id+"F0.wireOp",EDGE,"E256"),sQuery(id+"F0.wireOp",EDGE,"E257"),sQuery(id+"F0.wireOp",EDGE,"E258"),sQuery(id+"F0.wireOp",EDGE,"E259"),sQuery(id+"F0.wireOp",EDGE,"E260"),sQuery(id+"F0.wireOp",EDGE,"E261"),sQuery(id+"F0.wireOp",EDGE,"E262"),sQuery(id+"F0.wireOp",EDGE,"E263"),sQuery(id+"F0.wireOp",EDGE,"E264"),sQuery(id+"F0.wireOp",EDGE,"E265"),sQuery(id+"F0.wireOp",EDGE,"E266"),sQuery(id+"F0.wireOp",EDGE,"E267"),sQuery(id+"F0.wireOp",EDGE,"E268"),sQuery(id+"F0.wireOp",EDGE,"E269"),sQuery(id+"F0.wireOp",EDGE,"E270"),sQuery(id+"F0.wireOp",EDGE,"E271"),sQuery(id+"F0.wireOp",EDGE,"E272"),sQuery(id+"F0.wireOp",EDGE,"E273"),sQuery(id+"F0.wireOp",EDGE,"E276"),sQuery(id+"F0.wireOp",EDGE,"E281.top")])]});
            transform(context, id + "F17", {"entities" : qUnion([Q0]), "transformType" : TransformType.TRANSLATION_3D, "dx" : 0 * mm, "dy" : 0 * mm, "dz" : 0 * mm, "makeCopy" : true});
        }
        {
            var Q0;
            Q0=makeQuery(id+"F17.opPattern","COPY",BODY,{"derivedFrom":makeQuery(id+"F1.opExtrude","SWEPT_BODY",BODY,{"disambiguationData":[OSD([sQuery(id+"F0.wireOp",EDGE,"E204"),sQuery(id+"F0.wireOp",EDGE,"E206"),sQuery(id+"F0.wireOp",EDGE,"E207"),sQuery(id+"F0.wireOp",EDGE,"E208"),sQuery(id+"F0.wireOp",EDGE,"E209"),sQuery(id+"F0.wireOp",EDGE,"E210"),sQuery(id+"F0.wireOp",EDGE,"E211"),sQuery(id+"F0.wireOp",EDGE,"E212"),sQuery(id+"F0.wireOp",EDGE,"E213"),sQuery(id+"F0.wireOp",EDGE,"E214"),sQuery(id+"F0.wireOp",EDGE,"E215"),sQuery(id+"F0.wireOp",EDGE,"E216"),sQuery(id+"F0.wireOp",EDGE,"E217"),sQuery(id+"F0.wireOp",EDGE,"E218"),sQuery(id+"F0.wireOp",EDGE,"E219"),sQuery(id+"F0.wireOp",EDGE,"E220"),sQuery(id+"F0.wireOp",EDGE,"E221"),sQuery(id+"F0.wireOp",EDGE,"E222"),sQuery(id+"F0.wireOp",EDGE,"E223"),sQuery(id+"F0.wireOp",EDGE,"E224"),sQuery(id+"F0.wireOp",EDGE,"E225"),sQuery(id+"F0.wireOp",EDGE,"E226"),sQuery(id+"F0.wireOp",EDGE,"E227"),sQuery(id+"F0.wireOp",EDGE,"E228"),sQuery(id+"F0.wireOp",EDGE,"E229"),sQuery(id+"F0.wireOp",EDGE,"E230"),sQuery(id+"F0.wireOp",EDGE,"E231"),sQuery(id+"F0.wireOp",EDGE,"E232"),sQuery(id+"F0.wireOp",EDGE,"E233"),sQuery(id+"F0.wireOp",EDGE,"E234"),sQuery(id+"F0.wireOp",EDGE,"E235"),sQuery(id+"F0.wireOp",EDGE,"E236"),sQuery(id+"F0.wireOp",EDGE,"E237"),sQuery(id+"F0.wireOp",EDGE,"E238"),sQuery(id+"F0.wireOp",EDGE,"E239"),sQuery(id+"F0.wireOp",EDGE,"E240"),sQuery(id+"F0.wireOp",EDGE,"E241"),sQuery(id+"F0.wireOp",EDGE,"E242"),sQuery(id+"F0.wireOp",EDGE,"E243"),sQuery(id+"F0.wireOp",EDGE,"E244"),sQuery(id+"F0.wireOp",EDGE,"E245"),sQuery(id+"F0.wireOp",EDGE,"E246"),sQuery(id+"F0.wireOp",EDGE,"E247"),sQuery(id+"F0.wireOp",EDGE,"E248"),sQuery(id+"F0.wireOp",EDGE,"E249"),sQuery(id+"F0.wireOp",EDGE,"E250"),sQuery(id+"F0.wireOp",EDGE,"E251"),sQuery(id+"F0.wireOp",EDGE,"E252"),sQuery(id+"F0.wireOp",EDGE,"E253"),sQuery(id+"F0.wireOp",EDGE,"E254"),sQuery(id+"F0.wireOp",EDGE,"E255"),sQuery(id+"F0.wireOp",EDGE,"E256"),sQuery(id+"F0.wireOp",EDGE,"E257"),sQuery(id+"F0.wireOp",EDGE,"E258"),sQuery(id+"F0.wireOp",EDGE,"E259"),sQuery(id+"F0.wireOp",EDGE,"E260"),sQuery(id+"F0.wireOp",EDGE,"E261"),sQuery(id+"F0.wireOp",EDGE,"E262"),sQuery(id+"F0.wireOp",EDGE,"E263"),sQuery(id+"F0.wireOp",EDGE,"E264"),sQuery(id+"F0.wireOp",EDGE,"E265"),sQuery(id+"F0.wireOp",EDGE,"E266"),sQuery(id+"F0.wireOp",EDGE,"E267"),sQuery(id+"F0.wireOp",EDGE,"E268"),sQuery(id+"F0.wireOp",EDGE,"E269"),sQuery(id+"F0.wireOp",EDGE,"E270"),sQuery(id+"F0.wireOp",EDGE,"E271"),sQuery(id+"F0.wireOp",EDGE,"E272"),sQuery(id+"F0.wireOp",EDGE,"E273"),sQuery(id+"F0.wireOp",EDGE,"E276"),sQuery(id+"F0.wireOp",EDGE,"E281.top")])]}),"instanceName":"1"});
            deleteBodies(context, id + "F18", {"entities" : qUnion([Q0])});
        }
    });
